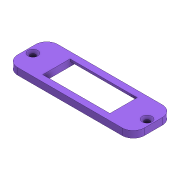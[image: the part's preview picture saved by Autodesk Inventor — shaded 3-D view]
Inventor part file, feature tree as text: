
AUTODESK INVENTOR PART (.ipt)
format: ipt  version: 2021 (Build 250183000, 183)  size: 111,104 bytes
history: native  units: mm
features: sketch x2, extrude x1, chamfer x1, hole x1, fillet x1
ambient origin geometry x8: Origin, YZ Plane, XZ Plane, XY Plane, X Axis, Y Axis, Z Axis, Center Point
bodies: Volumenkörper1 (feature_tree)
feature tree (6):
  extrude  "Extrusion1"  Depth=12.3mm
  chamfer  "Fase1"  Distance=18.0mm
  hole  "Bohrung1"  [1 undecoded]
  fillet  "Rundung1"  Radius=2.0mm
  sketch  "Skizze1"  dims[d0=30.2mm d1=12.3mm]
  sketch  "Skizze2"  dims[d2=56.9mm d3=18.0mm d4=3.0mm d5=0.0mm d6=2.0mm d7=2.0mm d8=45.0deg d9=25.65mm d10=51.3mm d11=2.4mm d12=6.0mm d13=4.4mm d14=2.0mm d15=90.0deg d16=8.0mm d17=20.594885mm d18=5.0mm]
note: 1 required parameter value undecoded (feature->parameter linkage not recoverable at this tier; creation-order binding heuristic only, values carry confidence <= 0.55)
